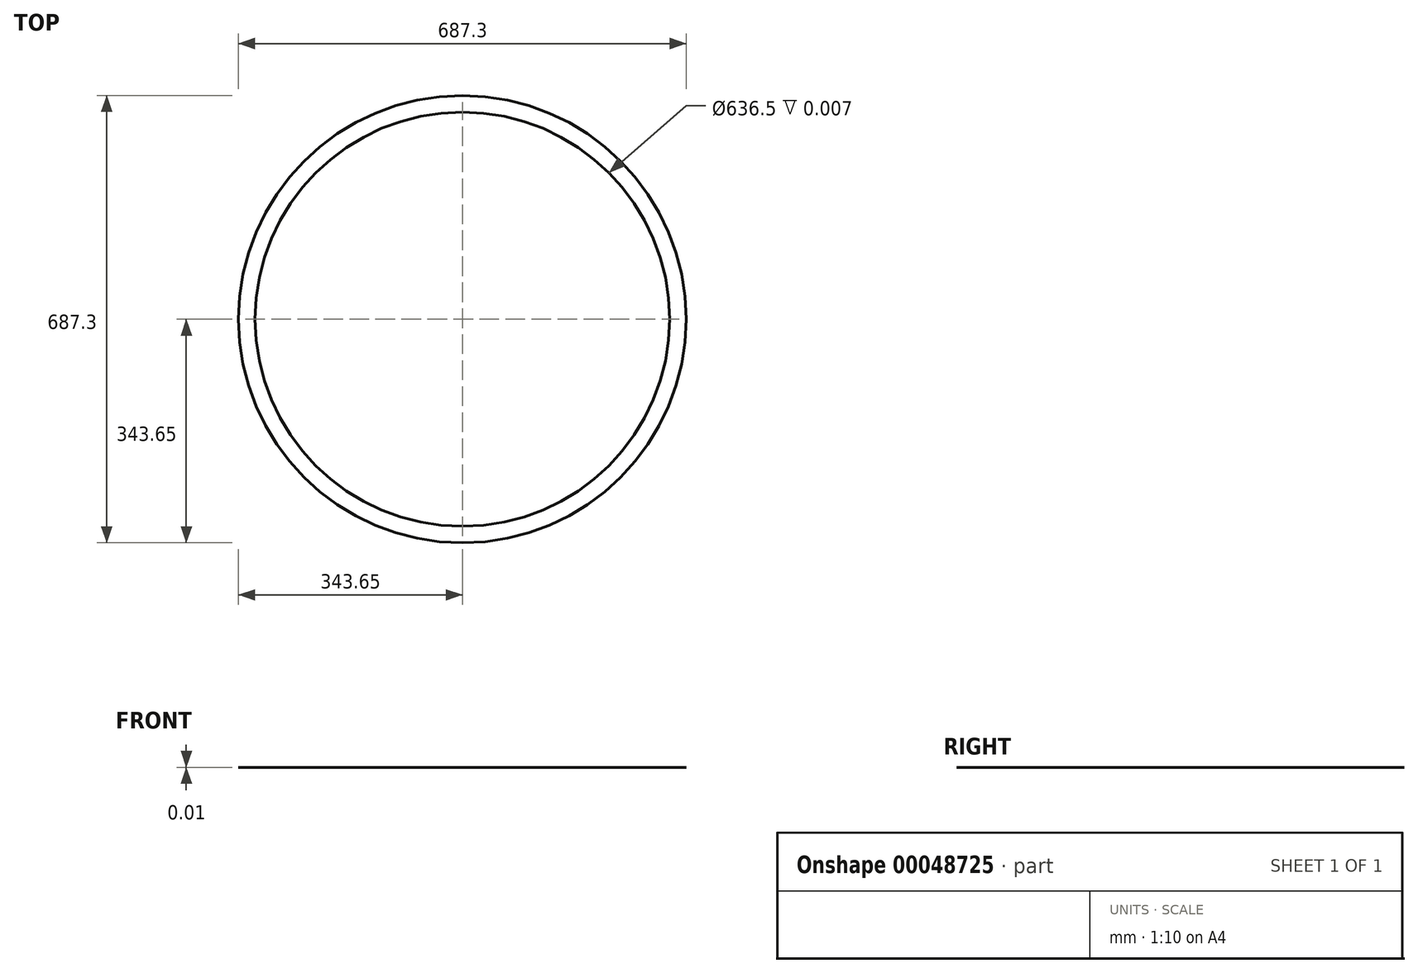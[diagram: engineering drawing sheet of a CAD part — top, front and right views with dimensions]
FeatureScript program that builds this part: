
annotation { "Feature Type Name" : "Feature", "Feature Type Description" : "" }
export const myFeature = defineFeature(function(context is Context, id is Id, definition is map)
    precondition{}
    {
        {
            var Q0;
            Q0=qCreatedBy(makeId("Top.planeOp"),FACE);
            var sketch = newSketch(context, id + "F0", { "sketchPlane" : qUnion([Q0])});
            skCircle(sketch, "E0", {"center": v(0, 0) * mm, "radius": 343.65 * mm});
            skCircle(sketch, "E1", {"center": v(0, 0) * mm, "radius": 318.25 * mm});
            skSolve(sketch);
        }
        {
            var Q0;
            Q0=makeQuery(id+"F0.imprint","IMPRINT",FACE,{"disambiguationData":[TD([[makeQuery(id+"F0.imprint","IMPRINT",EDGE,{"derivedFrom":sQuery(id+"F0.wireOp",EDGE,"E0")}),1.0]])]});
            extrude(context, id + "F1", {"entities" : qUnion([Q0]), "depth" : 3 / 406.4 * mm});
        }
    });
